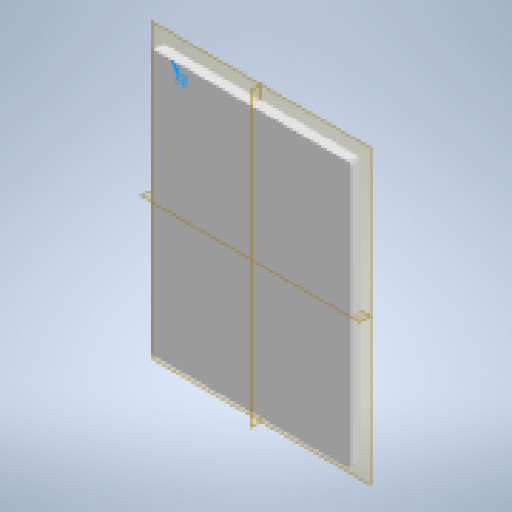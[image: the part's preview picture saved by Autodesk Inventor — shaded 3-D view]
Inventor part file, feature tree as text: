
AUTODESK INVENTOR PART (.ipt)
format: ipt  version: 2025.2 (Build 292293000, 293)  size: 241,152 bytes
history: native  units: in
note: dims shown in document units (in); Inventor stores cm internally (conversion verified against a paired STEP export)
features: fillet x3, sketch x3, extrude x2
ambient origin geometry x8: Origin, YZ Plane, XZ Plane, XY Plane, X Axis, Y Axis, Z Axis, Center Point
bodies: Solid1 (feature_tree)
feature tree (8):
  extrude  "Extrusion1"  Depth=31.4961in
  fillet  "Fillet1"  Radius=1.1811in
  fillet  "Fillet2"  Radius=0.3937in
  fillet  "Fillet3"  Radius=0.3937in
  sketch  "Sketch6"  dims[d13=0.3937in d29=1.9685in]
  sketch  "Sketch7"  dims[d30=2.3228in d31=1.1811in d32=0.0in]
  extrude  "Extrusion3"  Depth=0.3937in
  sketch  "Sketch1"  dims[d1=23.622in d2=31.4961in d3=1.1811in d4=0.0in d11=0.3937in d12=0.3937in]
